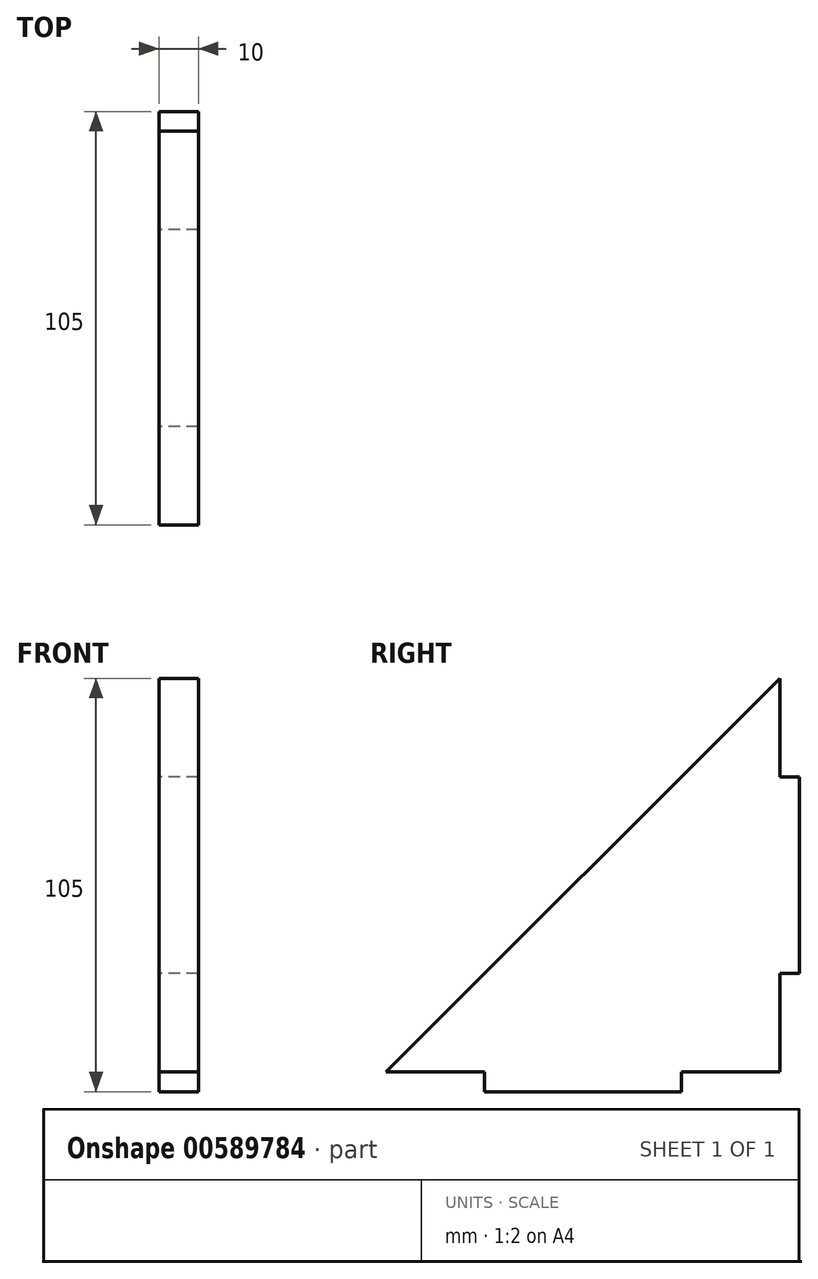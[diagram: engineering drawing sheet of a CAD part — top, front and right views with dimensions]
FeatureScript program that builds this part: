
annotation { "Feature Type Name" : "Feature", "Feature Type Description" : "" }
export const myFeature = defineFeature(function(context is Context, id is Id, definition is map)
    precondition{}
    {
        {
            var Q0;
            Q0=qCreatedBy(makeId("Right.planeOp"),FACE);
            var sketch = newSketch(context, id + "F0", { "sketchPlane" : qUnion([Q0])});
            skLineSegment(sketch, "E0", {"start": v(0, 0) * mm, "end": v(100, 100) * mm});
            skLineSegment(sketch, "E1", {"start": v(100, 100) * mm, "end": v(100, 0) * mm});
            skLineSegment(sketch, "E2", {"start": v(100, 0) * mm, "end": v(0, 0) * mm});
            skLineSegment(sketch, "E3.bottom", {"start": v(75, -5) * mm, "end": v(25, -5) * mm});
            skLineSegment(sketch, "E3.top", {"start": v(75, 5) * mm, "end": v(25, 5) * mm});
            skLineSegment(sketch, "E3.left", {"start": v(75, -5) * mm, "end": v(75, 5) * mm});
            skLineSegment(sketch, "E3.right", {"start": v(25, -5) * mm, "end": v(25, 5) * mm});
            skPoint(sketch, "E3.middle", {"position": v(50, 0) * mm});
            skLineSegment(sketch, "E4.bottom", {"start": v(105, 25) * mm, "end": v(95, 25) * mm});
            skLineSegment(sketch, "E4.top", {"start": v(105, 75) * mm, "end": v(95, 75) * mm});
            skLineSegment(sketch, "E4.left", {"start": v(105, 25) * mm, "end": v(105, 75) * mm});
            skLineSegment(sketch, "E4.right", {"start": v(95, 25) * mm, "end": v(95, 75) * mm});
            skPoint(sketch, "E4.middle", {"position": v(100, 50) * mm});
            skSolve(sketch);
        }
        {
            var Q0;
            {var subQ5=sQuery(id+"F0.wireOp",EDGE,"E4.left");Q0=makeQuery(id+"F0.imprint","IMPRINT",FACE,{"disambiguationData":[TD([[makeQuery(id+"F0.imprint","IMPRINT",EDGE,{"derivedFrom":subQ5}),1.0]])]});}
            var Q1;
            {var subQ5=sQuery(id+"F0.wireOp",EDGE,"E3.bottom");Q1=makeQuery(id+"F0.imprint","IMPRINT",FACE,{"disambiguationData":[TD([[makeQuery(id+"F0.imprint","IMPRINT",EDGE,{"derivedFrom":subQ5}),-1.0]])]});}
            var Q2;
            {var subQ8=sQuery(id+"F0.wireOp",EDGE,"E0");Q2=makeQuery(id+"F0.imprint","IMPRINT",FACE,{"disambiguationData":[TD([[makeQuery(id+"F0.imprint","IMPRINT",EDGE,{"derivedFrom":subQ8}),-1.0]])]});}
            var Q3;
            {var subQ5=sQuery(id+"F0.wireOp",EDGE,"E4.right");Q3=makeQuery(id+"F0.imprint","IMPRINT",FACE,{"disambiguationData":[TD([[makeQuery(id+"F0.imprint","IMPRINT",EDGE,{"derivedFrom":subQ5}),-1.0]])]});}
            var Q4;
            {var subQ5=sQuery(id+"F0.wireOp",EDGE,"E3.top");Q4=makeQuery(id+"F0.imprint","IMPRINT",FACE,{"disambiguationData":[TD([[makeQuery(id+"F0.imprint","IMPRINT",EDGE,{"derivedFrom":subQ5}),1.0]])]});}
            extrude(context, id + "F1", {"entities" : qUnion([Q0, Q1, Q2, Q3, Q4]), "depth" : 10 * mm, "offsetDistance" : 25 * mm});
        }
    });
